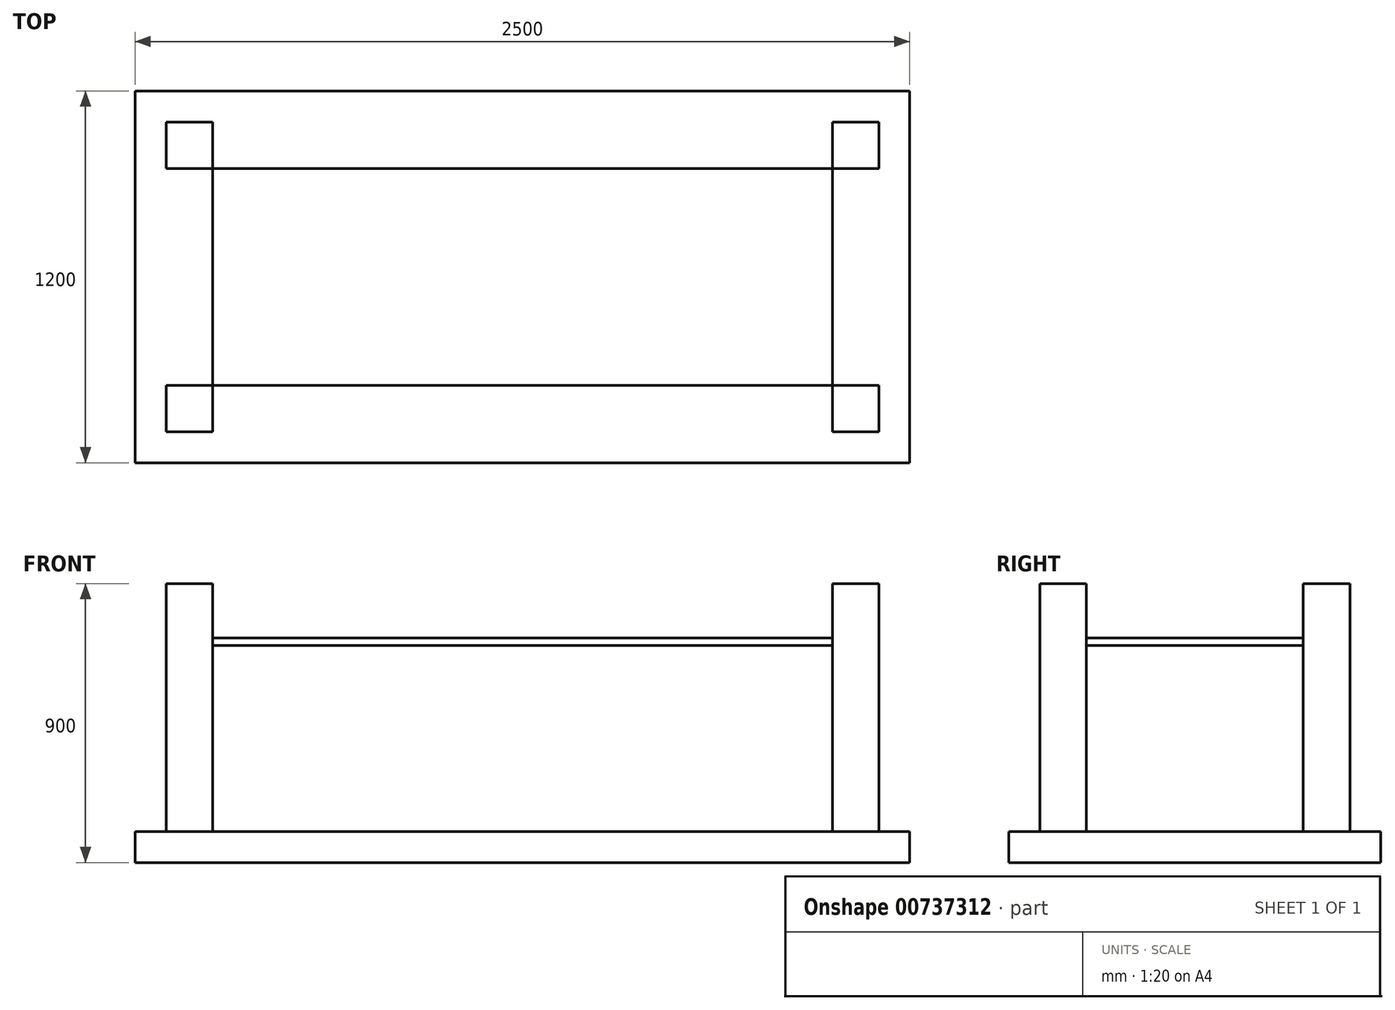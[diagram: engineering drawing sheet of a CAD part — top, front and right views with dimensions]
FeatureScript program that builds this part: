
annotation { "Feature Type Name" : "Feature", "Feature Type Description" : "" }
export const myFeature = defineFeature(function(context is Context, id is Id, definition is map)
    precondition{}
    {
        {
            var Q0;
            Q0=qCreatedBy(makeId("Front.planeOp"),FACE);
            var sketch = newSketch(context, id + "F0", { "sketchPlane" : qUnion([Q0])});
            skLineSegment(sketch, "E0.bottom", {"start": v(-1250.22, 101.59) * mm, "end": v(1249.78, 101.59) * mm});
            skLineSegment(sketch, "E0.top", {"start": v(-1250.22, 1.59) * mm, "end": v(1249.78, 1.59) * mm});
            skLineSegment(sketch, "E0.left", {"start": v(-1250.22, 101.59) * mm, "end": v(-1250.22, 1.59) * mm});
            skLineSegment(sketch, "E0.right", {"start": v(1249.78, 101.59) * mm, "end": v(1249.78, 1.59) * mm});
            skSolve(sketch);
        }
        {
            var Q0;
            Q0 = qSketchRegion(id + "F0", true);
            extrude(context, id + "F1", {"entities" : qUnion([Q0]), "depth" : 1200 * mm, "offsetDistance" : 25 * mm});
        }
        {
            var Q0;
            Q0=makeQuery(id+"F1.opExtrude","SWEPT_FACE",FACE,{"disambiguationData":[OSD([sQuery(id+"F0.wireOp",EDGE,"E0.bottom")])]});
            var sketch = newSketch(context, id + "F2", { "sketchPlane" : qUnion([Q0])});
            skLineSegment(sketch, "E1.bottom", {"start": v(-1150.22, -100) * mm, "end": v(-1000.22, -100) * mm});
            skLineSegment(sketch, "E1.top", {"start": v(-1150.22, -250) * mm, "end": v(-1000.22, -250) * mm});
            skLineSegment(sketch, "E1.left", {"start": v(-1150.22, -100) * mm, "end": v(-1150.22, -250) * mm});
            skLineSegment(sketch, "E1.right", {"start": v(-1000.22, -100) * mm, "end": v(-1000.22, -250) * mm});
            skLineSegment(sketch, "E2.0.1.0", {"start": v(-1000.22, -950) * mm, "end": v(-1000.22, -1100) * mm});
            skLineSegment(sketch, "E2.0.1.1", {"start": v(-1150.22, -950) * mm, "end": v(-1150.22, -1100) * mm});
            skLineSegment(sketch, "E2.0.1.2", {"start": v(-1150.22, -1100) * mm, "end": v(-1000.22, -1100) * mm});
            skLineSegment(sketch, "E2.0.1.3", {"start": v(-1150.22, -950) * mm, "end": v(-1000.22, -950) * mm});
            skLineSegment(sketch, "E2.1.0.0", {"start": v(1149.78, -100) * mm, "end": v(1149.78, -250) * mm});
            skLineSegment(sketch, "E2.1.0.1", {"start": v(999.78, -100) * mm, "end": v(999.78, -250) * mm});
            skLineSegment(sketch, "E2.1.0.2", {"start": v(999.78, -250) * mm, "end": v(1149.78, -250) * mm});
            skLineSegment(sketch, "E2.1.0.3", {"start": v(999.78, -100) * mm, "end": v(1149.78, -100) * mm});
            skLineSegment(sketch, "E2.1.1.0", {"start": v(1149.78, -950) * mm, "end": v(1149.78, -1100) * mm});
            skLineSegment(sketch, "E2.1.1.1", {"start": v(999.78, -950) * mm, "end": v(999.78, -1100) * mm});
            skLineSegment(sketch, "E2.1.1.2", {"start": v(999.78, -1100) * mm, "end": v(1149.78, -1100) * mm});
            skLineSegment(sketch, "E2.1.1.3", {"start": v(999.78, -950) * mm, "end": v(1149.78, -950) * mm});
            skLineSegment(sketch, "E2.direction1", {"start": v(-1150.22, -250) * mm, "end": v(999.78, -250) * mm, "construction": true});
            skLineSegment(sketch, "E2.direction2", {"start": v(-1150.22, -250) * mm, "end": v(-1150.22, -1100) * mm, "construction": true});
            skSolve(sketch);
        }
        {
            var Q0;
            Q0 = qSketchRegion(id + "F2", true);
            extrude(context, id + "F3", {"entities" : qUnion([Q0]), "operationType" : NewBodyOperationType.ADD, "depth" : 800 * mm, "offsetDistance" : 25 * mm});
        }
        {
            var Q0;
            Q0=makeQuery(id+"F1.opExtrude","SWEPT_FACE",FACE,{"disambiguationData":[OSD([sQuery(id+"F0.wireOp",EDGE,"E0.bottom")])]});
            cPlane(context, id + "F4", {"entities" : qUnion([Q0]), "cplaneType" : CPlaneType.OFFSET, "offset" : 600 * mm, "width" : 150 * mm, "height" : 150 * mm});
        }
        {
            var Q0;
            Q0=qCreatedBy(id+"F4.planeOp",FACE);
            var sketch = newSketch(context, id + "F5", { "sketchPlane" : qUnion([Q0])});
            skLineSegment(sketch, "E3.bottom", {"start": v(999.7, -950.02) * mm, "end": v(-1000.33, -950.02) * mm});
            skLineSegment(sketch, "E3.top", {"start": v(999.7, -250) * mm, "end": v(-1000.33, -250) * mm});
            skLineSegment(sketch, "E3.left", {"start": v(999.7, -950.02) * mm, "end": v(999.7, -250) * mm});
            skLineSegment(sketch, "E3.right", {"start": v(-1000.33, -950.02) * mm, "end": v(-1000.33, -250) * mm});
            skSolve(sketch);
        }
        {
            var Q0;
            Q0=makeQuery(id+"F5.imprint","IMPRINT",FACE,{"disambiguationData":[TD([[makeQuery(id+"F5.imprint","IMPRINT",EDGE,{"derivedFrom":sQuery(id+"F5.wireOp",EDGE,"E3.bottom")}),-1.0]])]});
            extrude(context, id + "F6", {"entities" : qUnion([Q0]), "operationType" : NewBodyOperationType.ADD, "depth" : 25 * mm, "offsetDistance" : 25 * mm});
        }
    });
